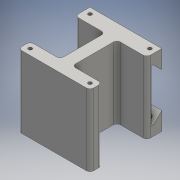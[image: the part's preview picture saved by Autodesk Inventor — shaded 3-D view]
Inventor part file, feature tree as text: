
AUTODESK INVENTOR PART (.ipt)
format: ipt  version: 2016 (Build 200138000, 138)  size: 178,176 bytes
history: native  units: mm
features: extrude x3, sketch x3, fillet x1
ambient origin geometry x8: Origin, YZ Plane, XZ Plane, XY Plane, X Axis, Y Axis, Z Axis, Center Point
bodies: Solid1 (feature_tree)
feature tree (7):
  extrude  "Block"  Depth=60.0mm
  extrude  "Tripod Slot"  Depth=5.0mm
  extrude  "Plastic Thinning"  Depth=3.0mm
  fillet  "Strength"  Radius=5.0mm
  sketch  "Sketch1"  dims[d0=60.0mm d1=60.0mm]
  sketch  "Sketch2"  dims[d2=5.0mm d3=5.0mm]
  sketch  "Sketch3"  dims[d4=5.0mm d5=5.0mm d6=5.0mm d7=5.0mm d8=5.0mm d9=5.0mm d10=3.0mm d11=3.0mm d12=3.0mm d13=3.0mm d14=60.0mm d15=0.0mm d17=14.75mm d18=14.75mm d19=8.9mm d20=21.75mm d21=21.75mm d22=2.0mm d23=2.0mm d24=60.0mm d25=0.0mm d26=5.0mm d27=90.0deg d28=5.0mm d29=90.0deg d30=7.5mm d31=90.0deg d32=7.5mm d33=90.0deg d34=25.0mm d35=25.0mm d36=25.0mm d37=25.0mm d38=90.0deg d39=90.0deg d40=4.861193mm d41=4.861193mm d42=55.0mm d43=60.0mm d44=0.0mm d45=3.0mm]
